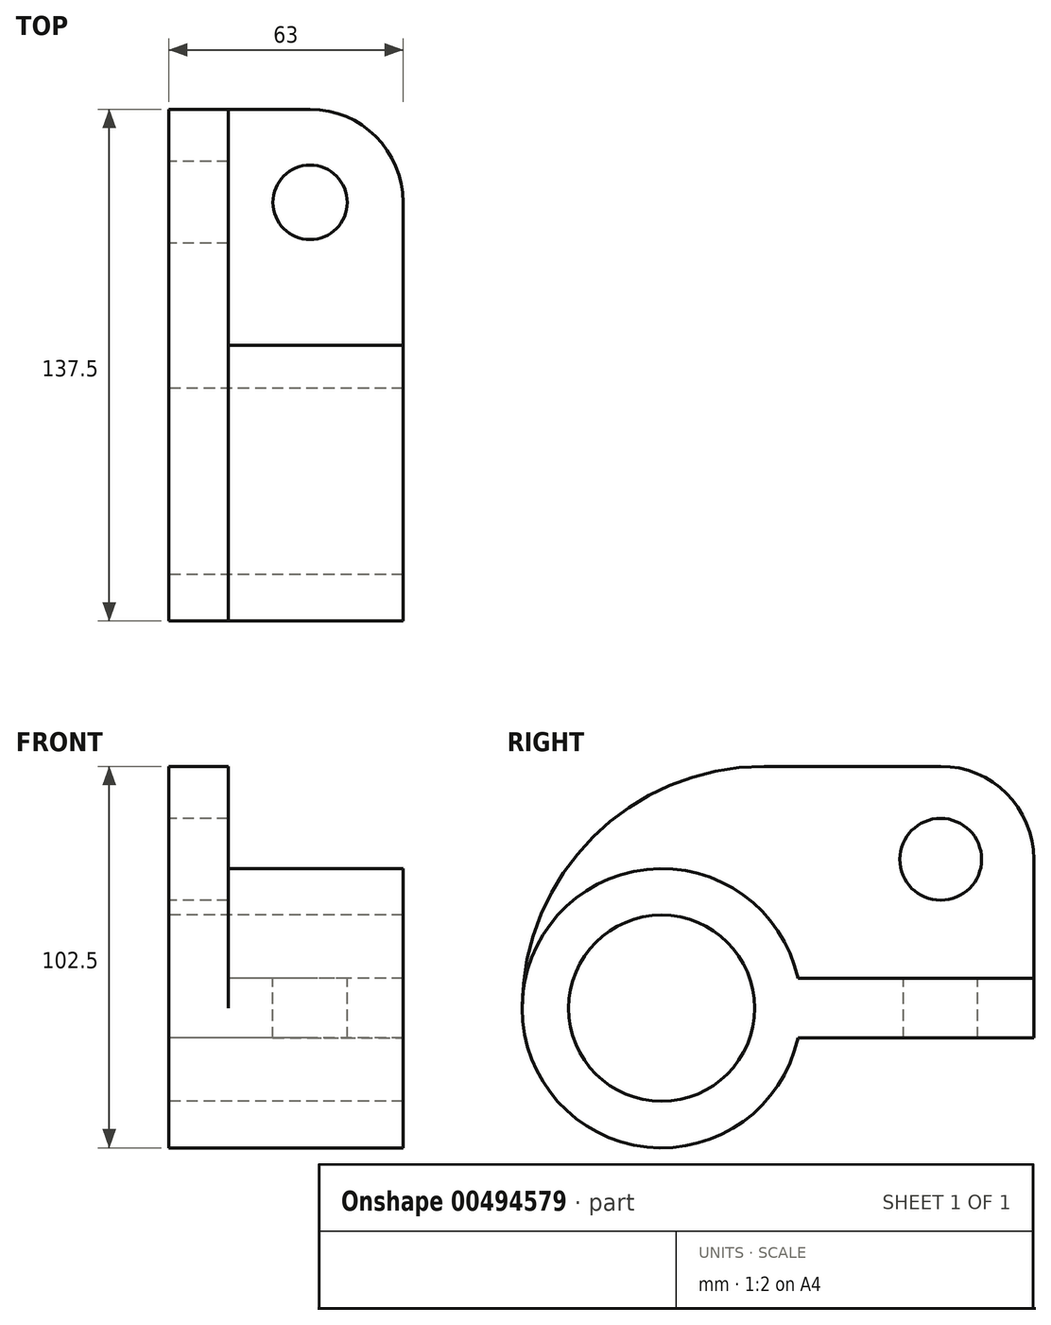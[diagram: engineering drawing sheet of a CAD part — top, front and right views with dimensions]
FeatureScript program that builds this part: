
annotation { "Feature Type Name" : "Feature", "Feature Type Description" : "" }
export const myFeature = defineFeature(function(context is Context, id is Id, definition is map)
    precondition{}
    {
        {
            var Q0;
            Q0=qCreatedBy(makeId("Right.planeOp"),FACE);
            var sketch = newSketch(context, id + "F0", { "sketchPlane" : qUnion([Q0])});
            skCircle(sketch, "E0", {"center": v(0, 0) * mm, "radius": 25 * mm});
            skArc(sketch, "E1", {"start": v(36.64, 8) * mm, "mid": v(-37.5, 0) * mm, "end": v(36.64, -8) * mm});
            skLineSegment(sketch, "E2", {"start": v(36.64, 8) * mm, "end": v(100, 8) * mm});
            skLineSegment(sketch, "E3", {"start": v(100, 8) * mm, "end": v(100, -8) * mm});
            skLineSegment(sketch, "E4", {"start": v(100, -8) * mm, "end": v(36.64, -8) * mm});
            skSolve(sketch);
        }
        {
            var Q0;
            Q0 = qSketchRegion(id + "F0", true);
            extrude(context, id + "F1", {"entities" : qUnion([Q0]), "depth" : 63 * mm});
        }
        {
            var Q0;
            Q0=makeQuery(id+"F1.opExtrude","CAP_FACE",FACE,{"disambiguationData":[OSD([sQuery(id+"F0.wireOp",EDGE,"E0"),sQuery(id+"F0.wireOp",EDGE,"E1"),sQuery(id+"F0.wireOp",EDGE,"E2"),sQuery(id+"F0.wireOp",EDGE,"E3"),sQuery(id+"F0.wireOp",EDGE,"E4")])],"isStart":true});
            var sketch = newSketch(context, id + "F2", { "sketchPlane" : qUnion([Q0])});
            skPoint(sketch, "E5.oppositeSnap0", {"position": v(37.5, 0) * mm});
            skLineSegment(sketch, "E5.top", {"start": v(-75, 65) * mm, "end": v(-27.5, 65) * mm});
            skLineSegment(sketch, "E5.left", {"start": v(-100, -8) * mm, "end": v(-100, 40) * mm});
            skArc(sketch, "E6", {"start": v(37.5, 0) * mm, "mid": v(18.46, 45.96) * mm, "end": v(-27.5, 65) * mm});
            skArc(sketch, "E7", {"start": v(-75, 65) * mm, "mid": v(-92.68, 57.68) * mm, "end": v(-100, 40) * mm});
            skCircle(sketch, "E8", {"center": v(-75, 40) * mm, "radius": 11 * mm});
            skPoint(sketch, "E5.right.end.orphan", {"position": v(37.5, 65) * mm});
            skSolve(sketch);
        }
        {
            var Q0;
            Q0=makeQuery(id+"F2.imprint","IMPRINT",FACE,{"disambiguationData":[TD([[makeQuery(id+"F2.imprint","IMPRINT",EDGE,{"derivedFrom":sQuery(id+"F2.wireOp",EDGE,"E5.top")}),-1.0]])]});
            extrude(context, id + "F3", {"entities" : qUnion([Q0]), "operationType" : NewBodyOperationType.ADD, "oppositeDirection" : true, "depth" : 16 * mm});
        }
        {
            var Q0;
            Q0=makeQuery(id+"F1.opExtrude","SWEPT_FACE",FACE,{"disambiguationData":[OSD([sQuery(id+"F0.wireOp",EDGE,"E2")])]});
            var sketch = newSketch(context, id + "F4", { "sketchPlane" : qUnion([Q0])});
            skCircle(sketch, "E9", {"center": v(38, 75) * mm, "radius": 10 * mm});
            skSolve(sketch);
        }
        {
            var Q0;
            Q0 = qSketchRegion(id + "F4", true);
            extrude(context, id + "F5", {"entities" : qUnion([Q0]), "operationType" : NewBodyOperationType.REMOVE, "oppositeDirection" : true, "depth" : 100 * mm});
        }
        {
            var Q0;
            Q0=makeQuery(id+"F1.opExtrude","CAP_EDGE",EDGE,{"disambiguationData":[OSD([sQuery(id+"F0.wireOp",EDGE,"E3")])],"isStart":false});
            fillet(context, id + "F6", {"entities" : qUnion([Q0]), "radius" : 25 * mm, "tangentPropagation" : true, "allowEdgeOverflow" : false});
        }
    });
